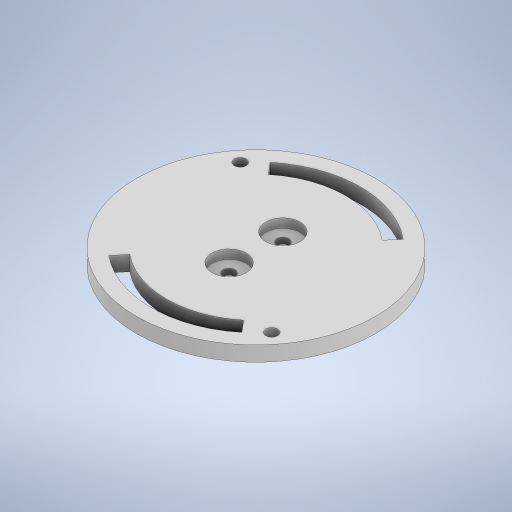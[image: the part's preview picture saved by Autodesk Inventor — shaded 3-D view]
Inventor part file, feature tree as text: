
AUTODESK INVENTOR PART (.ipt)
format: ipt  version: 2023 (Build 270158000, 158)  size: 309,248 bytes
history: native  units: in
note: dims shown in document units (in); Inventor stores cm internally (conversion verified against a paired STEP export)
features: extrude x6, sketch x5, plane x1, mirror x1
ambient origin geometry x8: Origin, YZ Plane, XZ Plane, XY Plane, X Axis, Y Axis, Z Axis, Center Point
bodies: Solid1 (feature_tree)
feature tree (13):
  extrude  "Extrusion1"  Depth=0.1969in TaperAngle=0.0deg
  extrude  "Extrusion3"  Depth=0.9843in
  extrude  "Extrusion5"  Depth=0.9843in
  extrude  "Extrusion7"  Depth=0.1575in TaperAngle=0.0deg
  plane  "Work Plane1"
  mirror  "Mirror1"
  extrude  "Extrusion10"  Depth=0.1969in
  extrude  "Extrusion11"  Depth=0.1181in
  sketch  "Sketch1"  dims[d0=3.1496in d1=0.1969in d2=0.0in]
  sketch  "Sketch6"  dims[d13=0.1969in d14=0.0in d18=0.9843in]
  sketch  "Sketch8"  dims[d19=0.9843in d20=0.7874in]
  sketch  "Sketch11"  dims[d21=0.7874in d22=0.1575in d23=0.0in]
  sketch  "Sketch12"  dims[d46=0.1969in d47=0.1969in d48=0.1181in d49=0.8933in d50=0.1575in d51=0.0in d63=0.3543in d64=0.3543in d65=0.1575in d66=0.1575in d67=0.4528in d68=0.4528in d69=0.1181in d70=0.0in d71=0.1969in d72=0.1969in d73=0.1575in d74=0.1969in d75=0.1969in d76=0.1575in d77=0.3937in d78=0.0in d10=0.0197in d11=0.0344in d12=0.0197in]
